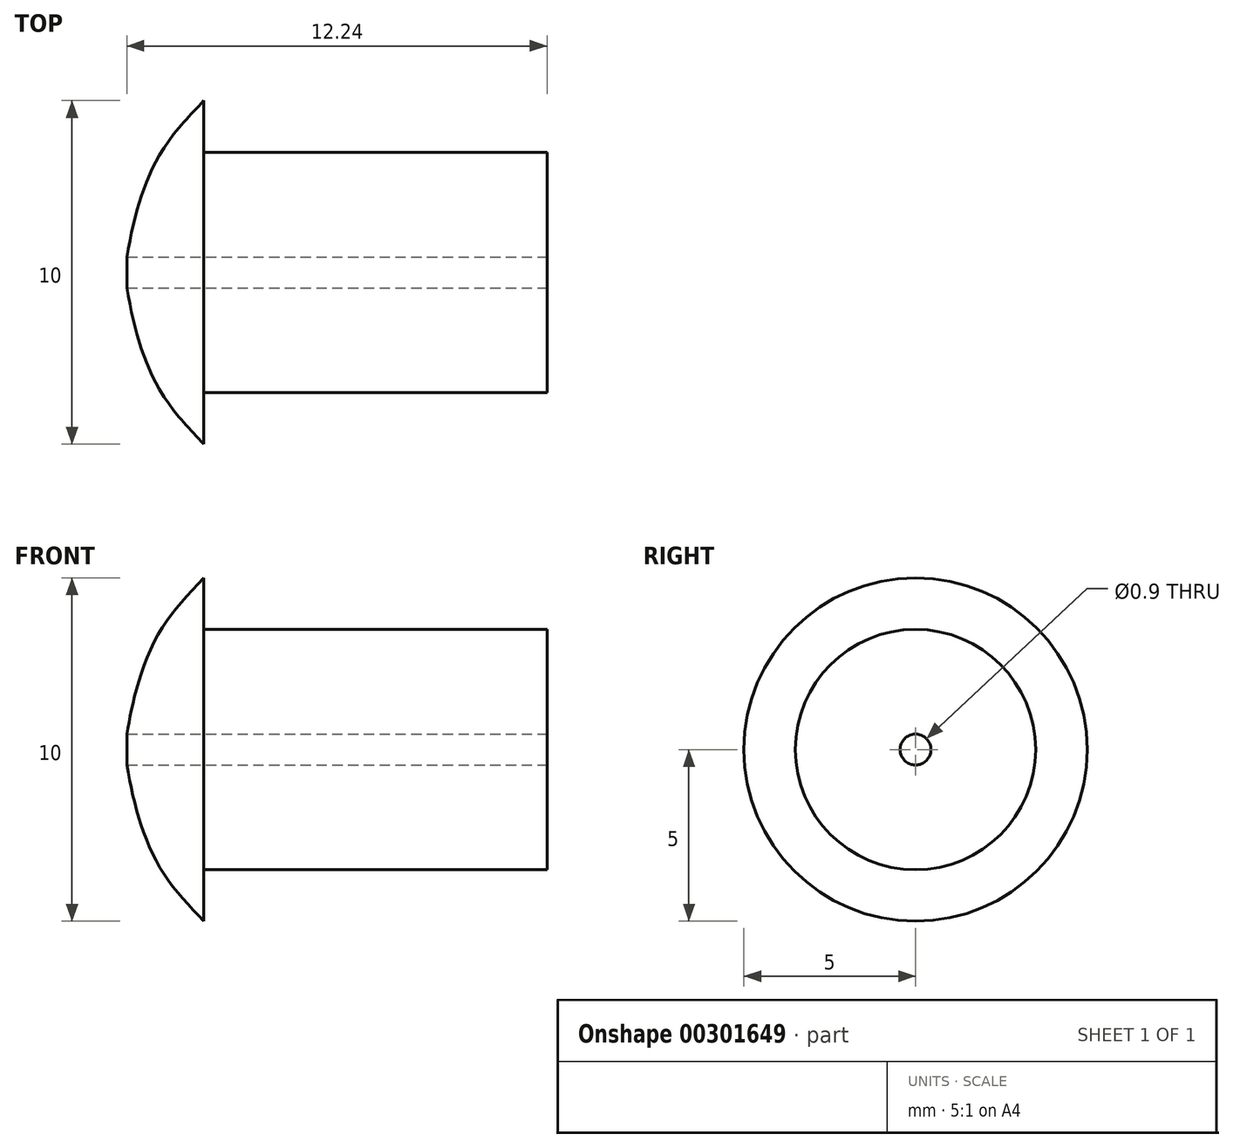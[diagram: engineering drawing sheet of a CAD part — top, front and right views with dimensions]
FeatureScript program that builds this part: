
annotation { "Feature Type Name" : "Feature", "Feature Type Description" : "" }
export const myFeature = defineFeature(function(context is Context, id is Id, definition is map)
    precondition{}
    {
        {
            var Q0;
            Q0=qCreatedBy(makeId("Front.planeOp"),FACE);
            var sketch = newSketch(context, id + "F0", { "sketchPlane" : qUnion([Q0])});
            skLineSegment(sketch, "E0", {"start": v(-8.92, 0) * mm, "end": v(13.71, 0) * mm, "construction": true});
            skLineSegment(sketch, "E1", {"start": v(0, 8.87) * mm, "end": v(0, -8.87) * mm, "construction": true});
            skLineSegment(sketch, "E2", {"start": v(0, 3.5) * mm, "end": v(10, 3.5) * mm});
            skLineSegment(sketch, "E3", {"start": v(0, 3.5) * mm, "end": v(0, 5) * mm});
            skLineSegment(sketch, "E4", {"start": v(10, 3.5) * mm, "end": v(10, 0) * mm});
            skLineSegment(sketch, "E5", {"start": v(10, 0) * mm, "end": v(-2.32, 0) * mm});
            skPoint(sketch, "E6.1.internal.orphan", {"position": v(-2.38, 3.5) * mm});
            skFitSpline(sketch, "E7", {"points": [v(-2.32, 0) * mm, v(-2.08, 1.29) * mm, v(-1.35, 3.32) * mm, v(0, 5) * mm], "startDerivative": vector(1, 5.25) * mm, "endDerivative": vector(4.32, 4.57) * mm});
            skSolve(sketch);
        }
        {
            var Q0;
            Q0=makeQuery(id+"F0.imprint","IMPRINT",FACE,{"disambiguationData":[TD([[makeQuery(id+"F0.imprint","IMPRINT",EDGE,{"derivedFrom":sQuery(id+"F0.wireOp",EDGE,"E2")}),-1.0]])]});
            var Q1;
            Q1=sQuery(id+"F0.wireOp",EDGE,"E0");
            revolve(context, id + "F1", {"entities" : qUnion([Q0]), "axis" : qUnion([Q1]), "revolveType" : RevolveType.FULL});
        }
        {
            var Q0;
            Q0=makeQuery(id+"F1.opRevolve","SWEPT_FACE",FACE,{"disambiguationData":[OSD([sQuery(id+"F0.wireOp",EDGE,"E4")])]});
            var sketch = newSketch(context, id + "F2", { "sketchPlane" : qUnion([Q0])});
            skCircle(sketch, "E8", {"center": v(0, 0) * mm, "radius": 0.45 * mm});
            skSolve(sketch);
        }
        {
            var Q0;
            Q0=makeQuery(id+"F2.imprint","IMPRINT",FACE,{"disambiguationData":[TD([[makeQuery(id+"F2.imprint","IMPRINT",EDGE,{"derivedFrom":sQuery(id+"F2.wireOp",EDGE,"E8")}),1.0]])]});
            extrude(context, id + "F3", {"entities" : qUnion([Q0]), "operationType" : NewBodyOperationType.REMOVE, "oppositeDirection" : true, "depth" : 25 * mm});
        }
    });
